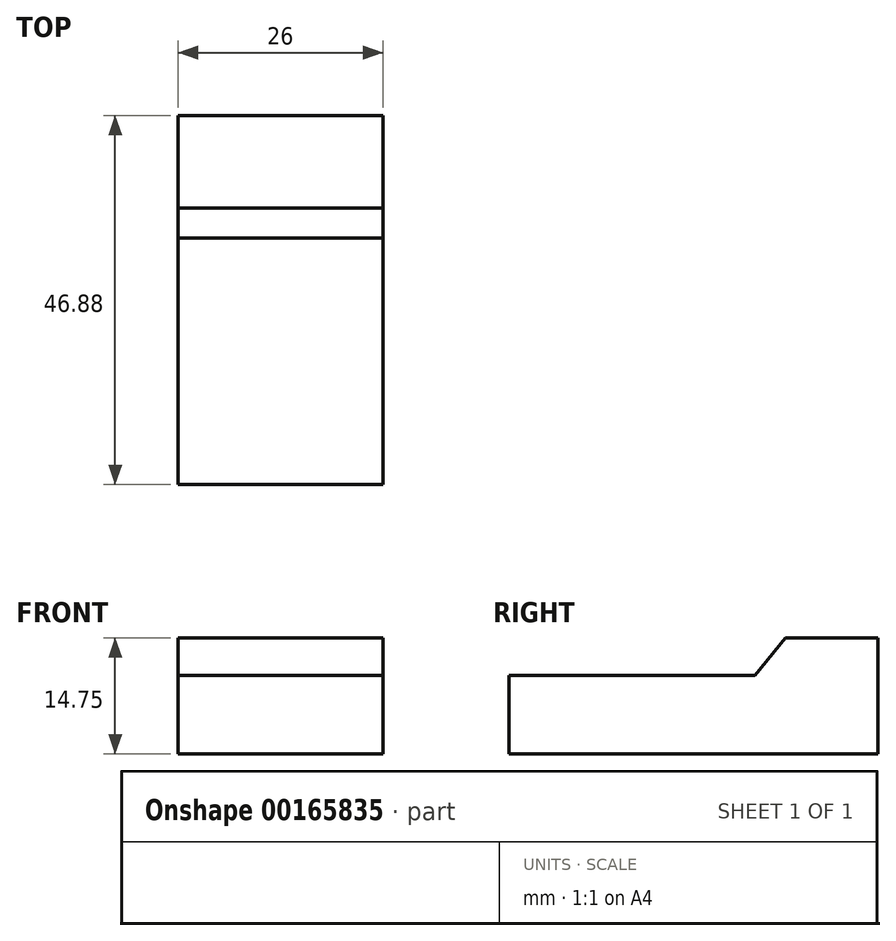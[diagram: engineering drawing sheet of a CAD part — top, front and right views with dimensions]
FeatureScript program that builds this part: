
annotation { "Feature Type Name" : "Feature", "Feature Type Description" : "" }
export const myFeature = defineFeature(function(context is Context, id is Id, definition is map)
    precondition{}
    {
        {
            var Q0;
            Q0=qCreatedBy(makeId("Right.planeOp"),FACE);
            var sketch = newSketch(context, id + "F0", { "sketchPlane" : qUnion([Q0])});
            skLineSegment(sketch, "E0", {"start": v(-23.43, 0) * mm, "end": v(23.43, 0) * mm});
            skLineSegment(sketch, "E1", {"start": v(23.43, 0) * mm, "end": v(23.43, 14.75) * mm});
            skLineSegment(sketch, "E2", {"start": v(23.43, 14.75) * mm, "end": v(11.68, 14.75) * mm});
            skLineSegment(sketch, "E3", {"start": v(11.68, 14.75) * mm, "end": v(7.84, 10) * mm});
            skLineSegment(sketch, "E4", {"start": v(7.84, 10) * mm, "end": v(-23.44, 10) * mm});
            skLineSegment(sketch, "E5", {"start": v(-23.44, 10) * mm, "end": v(-23.43, 0) * mm});
            skSolve(sketch);
        }
        {
            var Q0;
            Q0 = qSketchRegion(id + "F0", true);
            extrude(context, id + "F1", {"entities" : qUnion([Q0]), "endBound" : BoundingType.SYMMETRIC, "depth" : 26 * mm});
        }
    });
